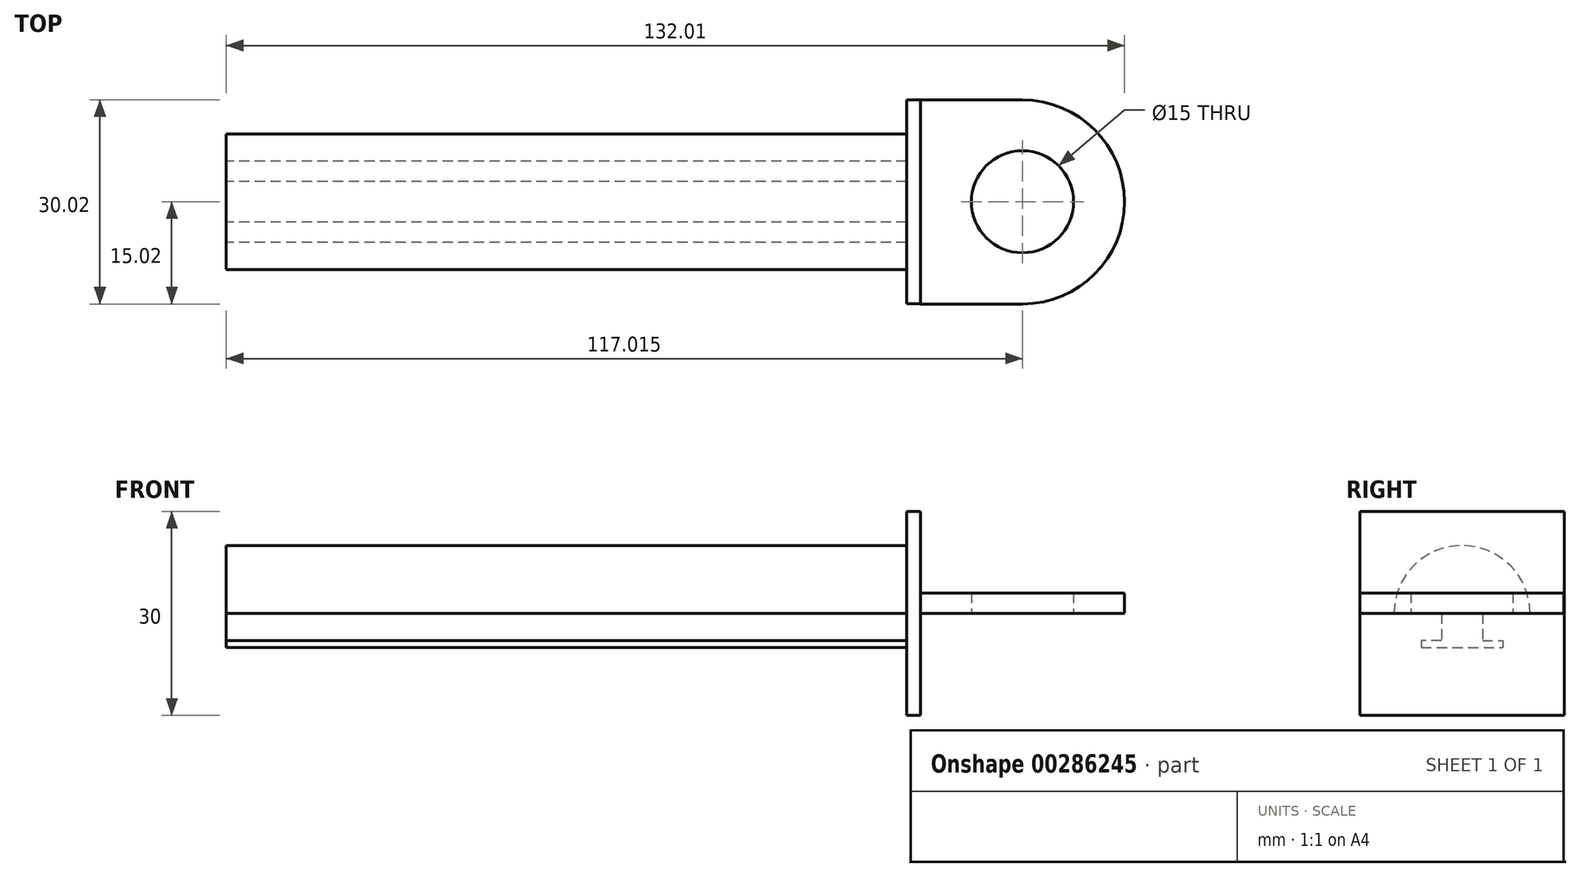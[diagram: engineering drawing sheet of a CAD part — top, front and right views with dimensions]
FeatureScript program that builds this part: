
annotation { "Feature Type Name" : "Feature", "Feature Type Description" : "" }
export const myFeature = defineFeature(function(context is Context, id is Id, definition is map)
    precondition{}
    {
        {
            var Q0;
            Q0=qCreatedBy(makeId("Right.planeOp"),FACE);
            var sketch = newSketch(context, id + "F0", { "sketchPlane" : qUnion([Q0])});
            skLineSegment(sketch, "E0", {"start": v(-10, 0) * mm, "end": v(10, 0) * mm, "construction": true});
            skArc(sketch, "E1", {"start": v(10, 0) * mm, "mid": v(0, 9.98) * mm, "end": v(-10, 0) * mm});
            skPoint(sketch, "E2", {"position": v(0, 9.98) * mm});
            skLineSegment(sketch, "E3", {"start": v(-10, 0) * mm, "end": v(-3, 0) * mm});
            skLineSegment(sketch, "E4", {"start": v(3, 0) * mm, "end": v(10, 0) * mm});
            skLineSegment(sketch, "E5", {"start": v(-3, 0) * mm, "end": v(-3, -4) * mm});
            skLineSegment(sketch, "E6", {"start": v(3, 0) * mm, "end": v(3, -4) * mm});
            skLineSegment(sketch, "E7", {"start": v(-3, -4) * mm, "end": v(-6, -4) * mm});
            skLineSegment(sketch, "E8", {"start": v(-6, -4) * mm, "end": v(-6, -5) * mm});
            skLineSegment(sketch, "E9", {"start": v(-6, -5) * mm, "end": v(6, -5) * mm});
            skLineSegment(sketch, "E10", {"start": v(3, -4) * mm, "end": v(6, -4) * mm});
            skLineSegment(sketch, "E11", {"start": v(6, -4) * mm, "end": v(6, -5) * mm});
            skSolve(sketch);
        }
        {
            var Q0;
            Q0 = qSketchRegion(id + "F0", true);
            extrude(context, id + "F1", {"entities" : qUnion([Q0]), "depth" : 100 * mm});
        }
        {
            var Q0;
            Q0=makeQuery(id+"F1.opExtrude","CAP_FACE",FACE,{"disambiguationData":[OSD([sQuery(id+"F0.wireOp",EDGE,"E1"),sQuery(id+"F0.wireOp",EDGE,"E3"),sQuery(id+"F0.wireOp",EDGE,"E4"),sQuery(id+"F0.wireOp",EDGE,"E5"),sQuery(id+"F0.wireOp",EDGE,"E6"),sQuery(id+"F0.wireOp",EDGE,"E7"),sQuery(id+"F0.wireOp",EDGE,"E8"),sQuery(id+"F0.wireOp",EDGE,"E9"),sQuery(id+"F0.wireOp",EDGE,"E10"),sQuery(id+"F0.wireOp",EDGE,"E11")])],"isStart":false});
            var sketch = newSketch(context, id + "F2", { "sketchPlane" : qUnion([Q0])});
            skLineSegment(sketch, "E12.bottom", {"start": v(15, -15) * mm, "end": v(-15, -15) * mm});
            skLineSegment(sketch, "E12.top", {"start": v(15, 15) * mm, "end": v(-15, 15) * mm});
            skLineSegment(sketch, "E12.left", {"start": v(15, -15) * mm, "end": v(15, 15) * mm});
            skLineSegment(sketch, "E12.right", {"start": v(-15, -15) * mm, "end": v(-15, 15) * mm});
            skPoint(sketch, "E12.middle", {"position": v(0, 0) * mm});
            skSolve(sketch);
        }
        {
            var Q0;
            Q0 = qSketchRegion(id + "F2", true);
            extrude(context, id + "F3", {"entities" : qUnion([Q0]), "operationType" : NewBodyOperationType.ADD, "depth" : 2 * mm});
        }
        {
            var Q0;
            Q0=makeQuery(id+"F3.opExtrude","CAP_FACE",FACE,{"disambiguationData":[OSD([sQuery(id+"F2.wireOp",EDGE,"E12.bottom"),sQuery(id+"F2.wireOp",EDGE,"E12.top"),sQuery(id+"F2.wireOp",EDGE,"E12.left"),sQuery(id+"F2.wireOp",EDGE,"E12.right")])],"isStart":false});
            var sketch = newSketch(context, id + "F4", { "sketchPlane" : qUnion([Q0])});
            skPoint(sketch, "E13", {"position": v(0, 0) * mm});
            skSolve(sketch);
        }
        {
            var Q0;
            Q0=sQuery(id+"F4.wireOp",VERTEX,"E13");
            var Q1;
            Q1=qCreatedBy(makeId("Top.planeOp"),FACE);
            cPlane(context, id + "F5", {"entities" : qUnion([Q0, Q1]), "cplaneType" : CPlaneType.PLANE_POINT, "offset" : 25 * mm, "width" : 150 * mm, "height" : 150 * mm});
        }
        {
            var Q0;
            Q0=qCreatedBy(id+"F5.planeOp",FACE);
            var sketch = newSketch(context, id + "F6", { "sketchPlane" : qUnion([Q0])});
            skLineSegment(sketch, "E14.bottom", {"start": v(102.01, 14.98) * mm, "end": v(117.01, 14.98) * mm});
            skLineSegment(sketch, "E14.top", {"start": v(102.01, -15.02) * mm, "end": v(117.01, -15.02) * mm});
            skLineSegment(sketch, "E14.left", {"start": v(102.01, 14.98) * mm, "end": v(102.01, -15.02) * mm});
            skLineSegment(sketch, "E14.right", {"start": v(117.01, 14.98) * mm, "end": v(117.01, -15.02) * mm});
            skCircle(sketch, "E15", {"center": v(117.01, 0) * mm, "radius": 7.5 * mm});
            skPoint(sketch, "E15.centerSnap0", {"position": v(117.01, -0.02) * mm});
            skArc(sketch, "E16", {"start": v(117.01, 14.98) * mm, "mid": v(132.01, -0.02) * mm, "end": v(117.01, -15.02) * mm});
            skSolve(sketch);
        }
        {
            var Q0;
            Q0 = qSketchRegion(id + "F6", true);
            extrude(context, id + "F7", {"entities" : qUnion([Q0]), "depth" : 3 * mm});
        }
    });
